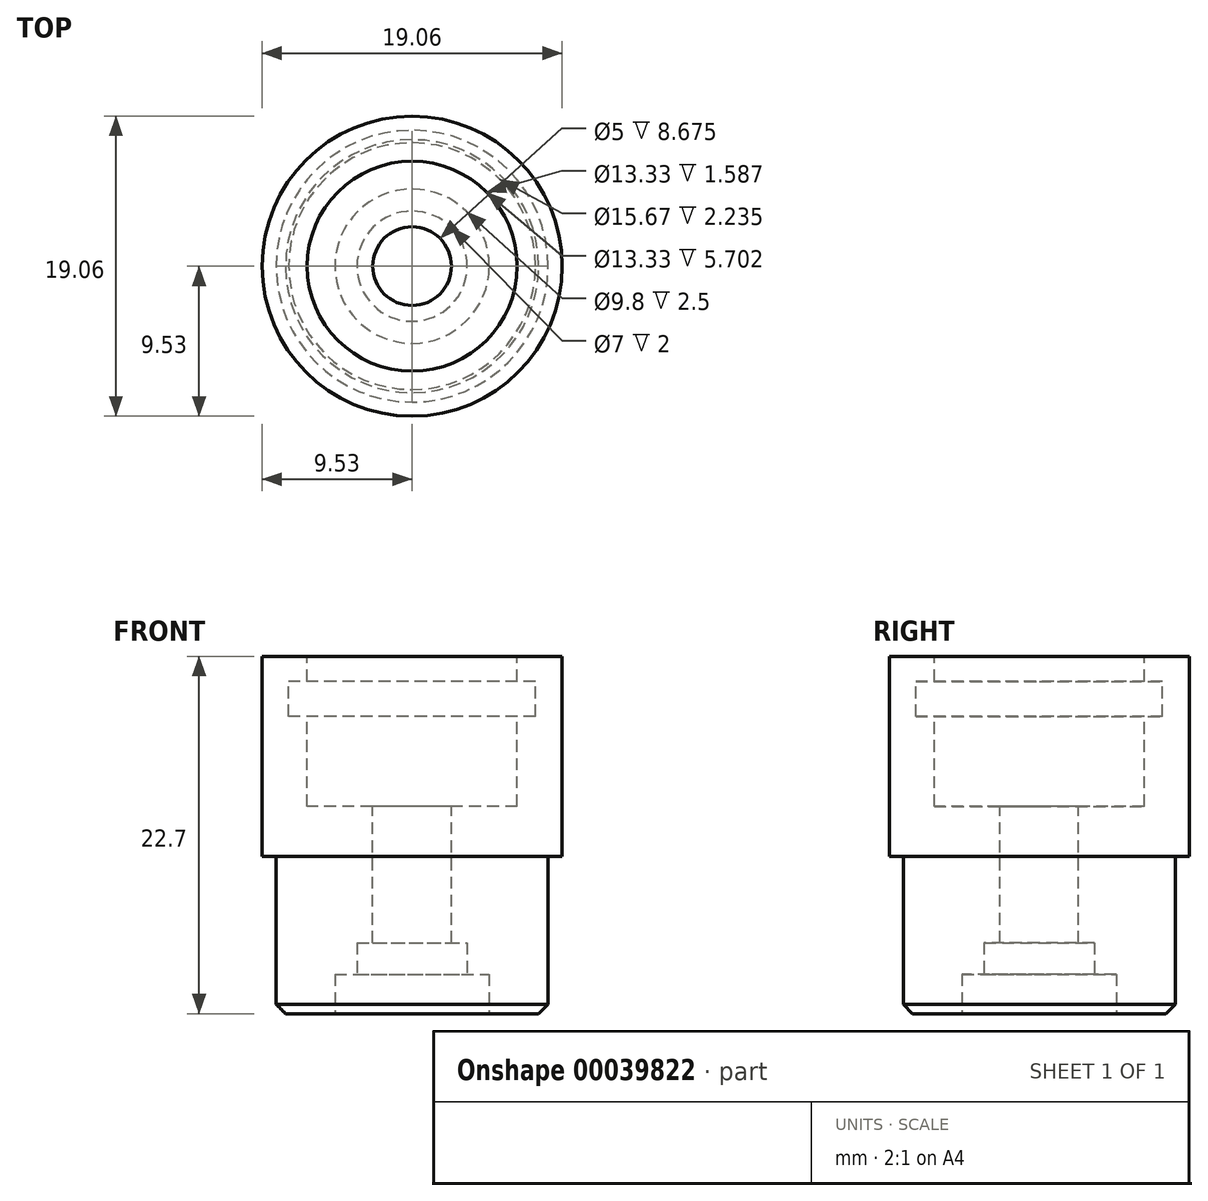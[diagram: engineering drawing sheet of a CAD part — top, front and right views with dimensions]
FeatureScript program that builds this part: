
annotation { "Feature Type Name" : "Feature", "Feature Type Description" : "" }
export const myFeature = defineFeature(function(context is Context, id is Id, definition is map)
    precondition{}
    {
        {
            var Q0;
            Q0=qCreatedBy(makeId("Top.planeOp"),FACE);
            var sketch = newSketch(context, id + "F0", { "sketchPlane" : qUnion([Q0])});
            skCircle(sketch, "E0", {"center": v(0, 0) * mm, "radius": 9.53 * mm});
            skSolve(sketch);
        }
        {
            var Q0;
            Q0=qSketchRegion(id+"F0",true);
            extrude(context, id + "F1", {"entities" : qUnion([Q0]), "depth" : 12.7 * mm});
        }
        {
            var Q0;
            Q0=makeQuery(id+"F1.opExtrude","CAP_FACE",FACE,{"disambiguationData":[OSD([sQuery(id+"F0.wireOp",EDGE,"E0")])],"isStart":false});
            var sketch = newSketch(context, id + "F2", { "sketchPlane" : qUnion([Q0])});
            skCircle(sketch, "E1", {"center": v(0, 0) * mm, "radius": 6.67 * mm});
            skSolve(sketch);
        }
        {
            var Q0;
            Q0=qSketchRegion(id+"F2",true);
            extrude(context, id + "F3", {"entities" : qUnion([Q0]), "operationType" : NewBodyOperationType.REMOVE, "oppositeDirection" : true, "depth" : 9.52 * mm});
        }
        {
            var Q0;
            Q0=qCreatedBy(makeId("Front.planeOp"),FACE);
            var sketch = newSketch(context, id + "F4", { "sketchPlane" : qUnion([Q0])});
            skLineSegment(sketch, "E2.bottom", {"start": v(6.67, 11.11) * mm, "end": v(7.84, 11.11) * mm});
            skLineSegment(sketch, "E2.top", {"start": v(6.67, 8.88) * mm, "end": v(7.84, 8.88) * mm});
            skLineSegment(sketch, "E2.left", {"start": v(6.67, 11.11) * mm, "end": v(6.67, 8.88) * mm});
            skLineSegment(sketch, "E2.right", {"start": v(7.84, 11.11) * mm, "end": v(7.84, 8.88) * mm});
            skLineSegment(sketch, "E3", {"start": v(0, 0) * mm, "end": v(0, 38.04) * mm, "construction": true});
            skSolve(sketch);
        }
        {
            var Q0;
            Q0=qSketchRegion(id+"F4",true);
            var Q1;
            Q1=sQuery(id+"F4.wireOp",EDGE,"E3");
            revolve(context, id + "F5", {"operationType" : NewBodyOperationType.REMOVE, "entities" : qUnion([Q0]), "axis" : qUnion([Q1]), "revolveType" : RevolveType.FULL, "oppositeDirection" : true});
        }
        {
            var Q0;
            Q0=makeQuery(id+"F1.opExtrude","CAP_FACE",FACE,{"disambiguationData":[OSD([sQuery(id+"F0.wireOp",EDGE,"E0")])],"isStart":true});
            var sketch = newSketch(context, id + "F6", { "sketchPlane" : qUnion([Q0])});
            skCircle(sketch, "E4", {"center": v(0, 0) * mm, "radius": 8.64 * mm});
            skSolve(sketch);
        }
        {
            var Q0;
            Q0=qSketchRegion(id+"F6",true);
            extrude(context, id + "F7", {"entities" : qUnion([Q0]), "operationType" : NewBodyOperationType.ADD, "offsetDistance" : 25 * mm, "depth" : 10 * mm});
        }
        {
            var Q0;
            Q0=makeQuery(id+"F7.opExtrude","CAP_FACE",FACE,{"disambiguationData":[OSD([sQuery(id+"F6.wireOp",EDGE,"E4")])],"isStart":false});
            var sketch = newSketch(context, id + "F8", { "sketchPlane" : qUnion([Q0])});
            skCircle(sketch, "E5", {"center": v(0, 0) * mm, "radius": 4.9 * mm});
            skSolve(sketch);
        }
        {
            var Q0;
            Q0=qSketchRegion(id+"F8",true);
            var Q1;
            Q1=makeQuery(id+"F1.opExtrude","CAP_FACE",FACE,{"disambiguationData":[OSD([sQuery(id+"F0.wireOp",EDGE,"E0")])],"isStart":true});
            extrude(context, id + "F9", {"entities" : qUnion([Q0]), "operationType" : NewBodyOperationType.REMOVE, "oppositeDirection" : true, "endBoundEntityFace" : qUnion([Q1]), "offsetDistance" : 25 * mm, "depth" : 2.5 * mm});
        }
        {
            var Q0;
            Q0=makeQuery(id+"F3.boolean.opBoolean","COPY",FACE,{"derivedFrom":makeQuery(id+"F3.opExtrude","CAP_FACE",FACE,{"disambiguationData":[OSD([sQuery(id+"F2.wireOp",EDGE,"E1")])],"isStart":false})});
            var sketch = newSketch(context, id + "F10", { "sketchPlane" : qUnion([Q0])});
            skCircle(sketch, "E6", {"center": v(0, 0) * mm, "radius": 2.5 * mm});
            skSolve(sketch);
        }
        {
            var Q0;
            Q0=qSketchRegion(id+"F10",true);
            extrude(context, id + "F11", {"entities" : qUnion([Q0]), "operationType" : NewBodyOperationType.REMOVE, "oppositeDirection" : true, "depth" : 25.4 * mm});
        }
        {
            var Q0;
            Q0=makeQuery(id+"F9.boolean.opBoolean","COPY",FACE,{"derivedFrom":makeQuery(id+"F9.opExtrude","CAP_FACE",FACE,{"disambiguationData":[OSD([sQuery(id+"F8.wireOp",EDGE,"E5")])],"isStart":false})});
            var sketch = newSketch(context, id + "F12", { "sketchPlane" : qUnion([Q0])});
            skCircle(sketch, "E7", {"center": v(0, 0) * mm, "radius": 3.5 * mm});
            skSolve(sketch);
        }
        {
            var Q0;
            Q0=qSketchRegion(id+"F12",true);
            extrude(context, id + "F13", {"entities" : qUnion([Q0]), "operationType" : NewBodyOperationType.REMOVE, "oppositeDirection" : true, "depth" : 2 * mm, "offsetDistance" : 25 * mm});
        }
        {
            var Q0;
            Q0=makeQuery(id+"F9.boolean.opBoolean","COPY",EDGE,{"derivedFrom":makeQuery(id+"F9.opExtrude","CAP_EDGE",EDGE,{"disambiguationData":[OSD([sQuery(id+"F8.wireOp",EDGE,"E5")])],"isStart":true})});
            var Q1;
            Q1=makeQuery(id+"F7.opExtrude","CAP_EDGE",EDGE,{"disambiguationData":[OSD([sQuery(id+"F6.wireOp",EDGE,"E4")])],"isStart":false});
            chamfer(context, id + "F14", {"entities" : qUnion([Q0, Q1]), "width" : .6 * mm, "tangentPropagation" : true});
        }
    });
